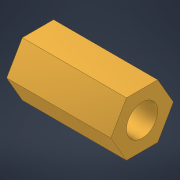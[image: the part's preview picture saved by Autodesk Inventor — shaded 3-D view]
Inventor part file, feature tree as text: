
AUTODESK INVENTOR PART (.ipt)
format: ipt  version: 2022 (Build 260153000, 153)  size: 96,768 bytes
history: native  units: mm
features: extrude x1, sketch x1
ambient origin geometry x8: Origin, YZ Plane, XZ Plane, XY Plane, X Axis, Y Axis, Z Axis, Center Point
bodies: Solid1 (feature_tree)
feature tree (2):
  extrude  "Extrusion1"  Depth=3.0mm
  sketch  "Sketch1"  dims[d0=6.0mm d1=3.0mm d2=10.0mm d3=0.0mm]
